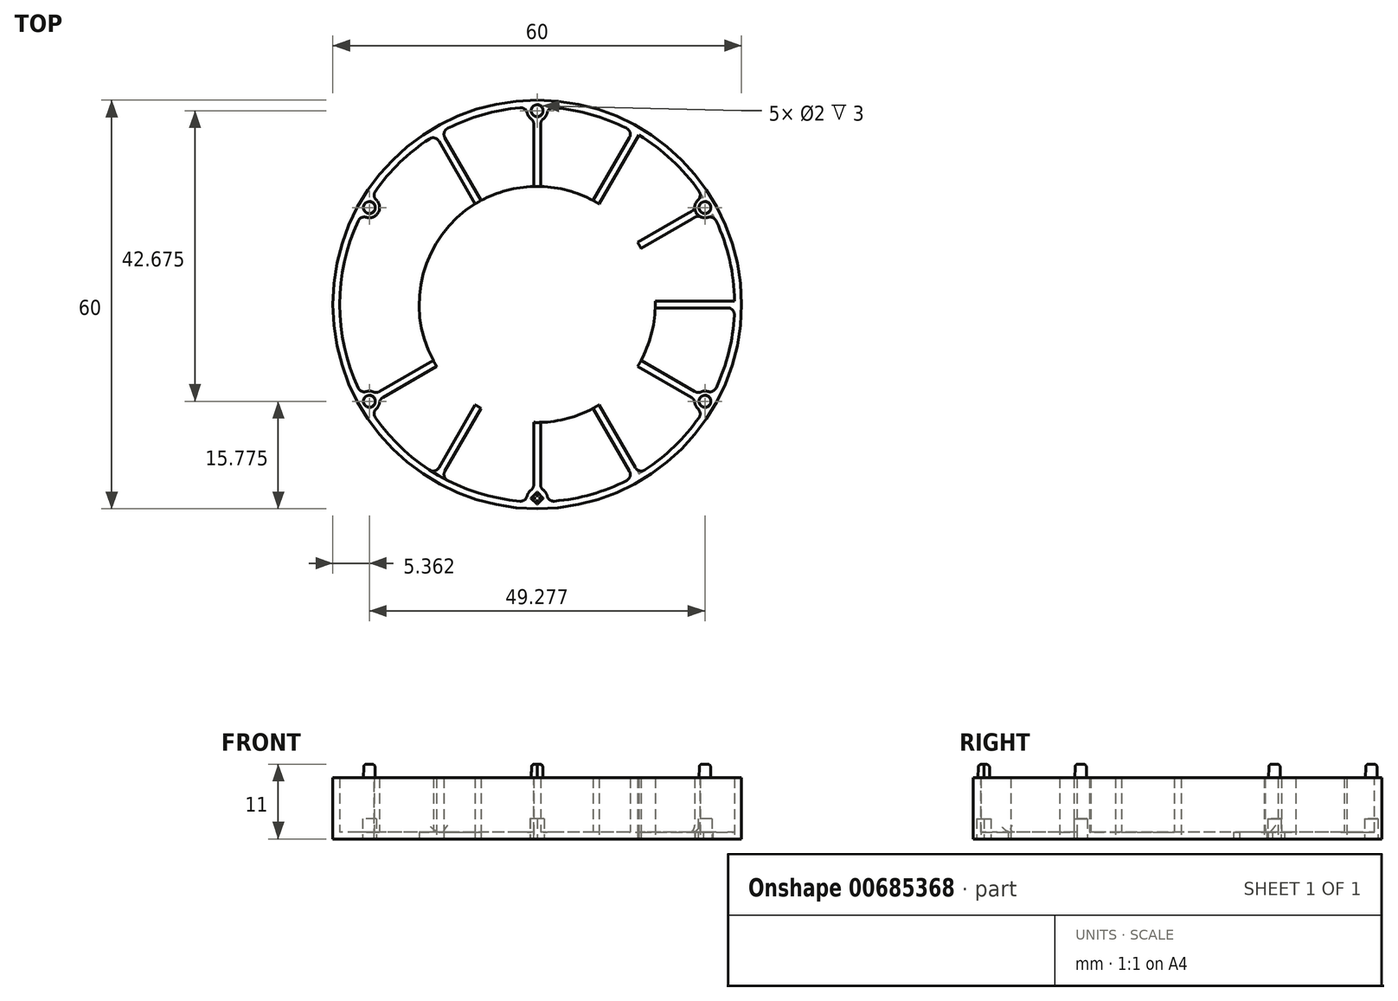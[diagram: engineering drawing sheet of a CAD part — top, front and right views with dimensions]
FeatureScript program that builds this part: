
annotation { "Feature Type Name" : "Feature", "Feature Type Description" : "" }
export const myFeature = defineFeature(function(context is Context, id is Id, definition is map)
    precondition{}
    {
        {
            var Q0;
            Q0=qCreatedBy(makeId("Top.planeOp"),FACE);
            var sketch = newSketch(context, id + "F0", { "sketchPlane" : qUnion([Q0])});
            skCircle(sketch, "E0", {"center": v(0, 0) * mm, "radius": 30 * mm});
            skCircle(sketch, "E1.0", {"center": v(0, 0) * mm, "radius": 29 * mm});
            skLineSegment(sketch, "E2.bottom", {"start": v(14.56, 26.23) * mm, "end": v(15.43, 25.73) * mm});
            skLineSegment(sketch, "E2.top", {"start": v(-15.43, -25.73) * mm, "end": v(-14.56, -26.23) * mm});
            skLineSegment(sketch, "E2.left", {"start": v(14.56, 26.23) * mm, "end": v(-15.43, -25.73) * mm});
            skLineSegment(sketch, "E2.right", {"start": v(15.43, 25.73) * mm, "end": v(-14.56, -26.23) * mm});
            skLineSegment(sketch, "E3.bottom", {"start": v(25.73, 15.43) * mm, "end": v(26.23, 14.56) * mm});
            skLineSegment(sketch, "E3.top", {"start": v(-26.23, -14.56) * mm, "end": v(-25.73, -15.43) * mm});
            skLineSegment(sketch, "E3.left", {"start": v(25.73, 15.43) * mm, "end": v(-26.23, -14.56) * mm});
            skLineSegment(sketch, "E3.right", {"start": v(26.23, 14.56) * mm, "end": v(-25.73, -15.43) * mm});
            skLineSegment(sketch, "E4", {"start": v(-38.35, 0) * mm, "end": v(39.17, 0) * mm, "construction": true});
            skLineSegment(sketch, "E5", {"start": v(0, 42.5) * mm, "end": v(0, -42.47) * mm, "construction": true});
            skLineSegment(sketch, "E6.bottom", {"start": v(-30, 0.5) * mm, "end": v(30, 0.5) * mm});
            skLineSegment(sketch, "E6.top", {"start": v(-30, -0.5) * mm, "end": v(30, -0.5) * mm});
            skLineSegment(sketch, "E6.left", {"start": v(-30, 0.5) * mm, "end": v(-30, -0.5) * mm});
            skLineSegment(sketch, "E6.right", {"start": v(30, 0.5) * mm, "end": v(30, -0.5) * mm});
            skLineSegment(sketch, "E7.bottom", {"start": v(-25.73, 15.43) * mm, "end": v(26.23, -14.56) * mm});
            skLineSegment(sketch, "E7.top", {"start": v(-26.23, 14.56) * mm, "end": v(25.73, -15.43) * mm});
            skLineSegment(sketch, "E7.left", {"start": v(-25.73, 15.43) * mm, "end": v(-26.23, 14.56) * mm});
            skLineSegment(sketch, "E7.right", {"start": v(26.23, -14.56) * mm, "end": v(25.73, -15.43) * mm});
            skLineSegment(sketch, "E8.bottom", {"start": v(-0.5, 30) * mm, "end": v(0.5, 30) * mm});
            skLineSegment(sketch, "E8.top", {"start": v(-0.5, -30) * mm, "end": v(0.5, -30) * mm});
            skLineSegment(sketch, "E8.left", {"start": v(-0.5, 30) * mm, "end": v(-0.5, -30) * mm});
            skLineSegment(sketch, "E8.right", {"start": v(0.5, 30) * mm, "end": v(0.5, -30) * mm});
            skLineSegment(sketch, "E9.bottom", {"start": v(-15.43, 25.73) * mm, "end": v(-14.56, 26.23) * mm});
            skLineSegment(sketch, "E9.top", {"start": v(14.56, -26.23) * mm, "end": v(15.43, -25.73) * mm});
            skLineSegment(sketch, "E9.left", {"start": v(-15.43, 25.73) * mm, "end": v(14.56, -26.23) * mm});
            skLineSegment(sketch, "E9.right", {"start": v(-14.56, 26.23) * mm, "end": v(15.43, -25.73) * mm});
            skCircle(sketch, "E10", {"center": v(0, 0) * mm, "radius": 17.33 * mm});
            skSolve(sketch);
        }
        {
            var Q0;
            Q0=qCreatedBy(makeId("Top.planeOp"),FACE);
            var sketch = newSketch(context, id + "F1", { "sketchPlane" : qUnion([Q0])});
            skCircle(sketch, "E11", {"center": v(0, 0) * mm, "radius": 30 * mm});
            skCircle(sketch, "E12", {"center": v(0, 0) * mm, "radius": 29 * mm});
            skSolve(sketch);
        }
        {
            var Q0;
            Q0=makeQuery(id+"F1.imprint","IMPRINT",FACE,{"disambiguationData":[TD([[makeQuery(id+"F1.imprint","IMPRINT",EDGE,{"derivedFrom":sQuery(id+"F1.wireOp",EDGE,"E11")}),1.0]])]});
            extrude(context, id + "F2", {"entities" : qUnion([Q0]), "depth" : 9 * mm, "offsetDistance" : 25 * mm});
        }
        {
            var Q0;
            {var subQ0=sQuery(id+"F0.wireOp",EDGE,"E2.right");var subQ1=sQuery(id+"F0.wireOp",EDGE,"E1.0");var subQ2=makeQuery(id+"F0.imprint","INTERSECT",VERTEX,{"disambiguationData":[OD(0.0)],"derivedFrom":[subQ1,subQ0]});Q0=makeQuery(id+"F0.imprint","IMPRINT",FACE,{"disambiguationData":[TD([[makeQuery(id+"F0.imprint","IMPRINT",EDGE,{"disambiguationData":[TD([[subQ2,-1.0]])],"derivedFrom":subQ1}),1.0]])]});}
            var Q1;
            {var subQ0=sQuery(id+"F0.wireOp",EDGE,"E6.bottom");var subQ1=sQuery(id+"F0.wireOp",EDGE,"E1.0");var subQ2=makeQuery(id+"F0.imprint","INTERSECT",VERTEX,{"disambiguationData":[OD(0.0)],"derivedFrom":[subQ1,subQ0]});Q1=makeQuery(id+"F0.imprint","IMPRINT",FACE,{"disambiguationData":[TD([[makeQuery(id+"F0.imprint","IMPRINT",EDGE,{"disambiguationData":[TD([[subQ2,1.0]])],"derivedFrom":subQ1}),1.0]])]});}
            var Q2;
            {var subQ0=sQuery(id+"F0.wireOp",EDGE,"E8.left");var subQ1=sQuery(id+"F0.wireOp",EDGE,"E1.0");var subQ2=makeQuery(id+"F0.imprint","INTERSECT",VERTEX,{"disambiguationData":[OD(1.0)],"derivedFrom":[subQ1,subQ0]});Q2=makeQuery(id+"F0.imprint","IMPRINT",FACE,{"disambiguationData":[TD([[makeQuery(id+"F0.imprint","IMPRINT",EDGE,{"disambiguationData":[TD([[subQ2,-1.0]])],"derivedFrom":subQ1}),1.0]])]});}
            var Q3;
            {var subQ0=sQuery(id+"F0.wireOp",EDGE,"E3.left");var subQ1=sQuery(id+"F0.wireOp",EDGE,"E1.0");var subQ2=makeQuery(id+"F0.imprint","INTERSECT",VERTEX,{"disambiguationData":[OD(1.0)],"derivedFrom":[subQ1,subQ0]});Q3=makeQuery(id+"F0.imprint","IMPRINT",FACE,{"disambiguationData":[TD([[makeQuery(id+"F0.imprint","IMPRINT",EDGE,{"disambiguationData":[TD([[subQ2,-1.0]])],"derivedFrom":subQ1}),1.0]])]});}
            var Q4;
            {var subQ0=sQuery(id+"F0.wireOp",EDGE,"E9.right");var subQ1=sQuery(id+"F0.wireOp",EDGE,"E1.0");var subQ2=makeQuery(id+"F0.imprint","INTERSECT",VERTEX,{"disambiguationData":[OD(0.0)],"derivedFrom":[subQ1,subQ0]});Q4=makeQuery(id+"F0.imprint","IMPRINT",FACE,{"disambiguationData":[TD([[makeQuery(id+"F0.imprint","IMPRINT",EDGE,{"disambiguationData":[TD([[subQ2,-1.0]])],"derivedFrom":subQ1}),1.0]])]});}
            var Q5;
            {var subQ0=sQuery(id+"F0.wireOp",EDGE,"E8.right");var subQ1=sQuery(id+"F0.wireOp",EDGE,"E1.0");var subQ2=makeQuery(id+"F0.imprint","INTERSECT",VERTEX,{"disambiguationData":[OD(0.0)],"derivedFrom":[subQ1,subQ0]});Q5=makeQuery(id+"F0.imprint","IMPRINT",FACE,{"disambiguationData":[TD([[makeQuery(id+"F0.imprint","IMPRINT",EDGE,{"disambiguationData":[TD([[subQ2,-1.0]])],"derivedFrom":subQ1}),1.0]])]});}
            var Q6;
            {var subQ0=sQuery(id+"F0.wireOp",EDGE,"E7.top");var subQ1=sQuery(id+"F0.wireOp",EDGE,"E1.0");var subQ2=makeQuery(id+"F0.imprint","INTERSECT",VERTEX,{"disambiguationData":[OD(1.0)],"derivedFrom":[subQ1,subQ0]});Q6=makeQuery(id+"F0.imprint","IMPRINT",FACE,{"disambiguationData":[TD([[makeQuery(id+"F0.imprint","IMPRINT",EDGE,{"disambiguationData":[TD([[subQ2,-1.0]])],"derivedFrom":subQ1}),1.0]])]});}
            var Q7;
            {var subQ0=sQuery(id+"F0.wireOp",EDGE,"E9.left");var subQ1=sQuery(id+"F0.wireOp",EDGE,"E1.0");var subQ2=makeQuery(id+"F0.imprint","INTERSECT",VERTEX,{"disambiguationData":[OD(1.0)],"derivedFrom":[subQ1,subQ0]});Q7=makeQuery(id+"F0.imprint","IMPRINT",FACE,{"disambiguationData":[TD([[makeQuery(id+"F0.imprint","IMPRINT",EDGE,{"disambiguationData":[TD([[subQ2,-1.0]])],"derivedFrom":subQ1}),1.0]])]});}
            extrude(context, id + "F3", {"entities" : qUnion([Q0, Q1, Q2, Q3, Q4, Q5, Q6, Q7]), "operationType" : NewBodyOperationType.ADD, "depth" : 9 * mm, "offsetDistance" : 25 * mm});
        }
        {
            var Q0;
            Q0=makeQuery(id+"F1.imprint","IMPRINT",FACE,{"disambiguationData":[TD([[makeQuery(id+"F1.imprint","IMPRINT",EDGE,{"derivedFrom":sQuery(id+"F1.wireOp",EDGE,"E11")}),1.0]])]});
            var Q1;
            Q1=makeQuery(id+"F1.imprint","IMPRINT",FACE,{"disambiguationData":[TD([[makeQuery(id+"F1.imprint","IMPRINT",EDGE,{"derivedFrom":sQuery(id+"F1.wireOp",EDGE,"E12")}),1.0]])]});
            extrude(context, id + "F4", {"entities" : qUnion([Q0, Q1]), "operationType" : NewBodyOperationType.ADD, "depth" : 1 * mm, "offsetDistance" : 25 * mm});
        }
        {
            var Q0;
            {var subQ0=sQuery(id+"F0.wireOp",EDGE,"E9.right");var subQ1=sQuery(id+"F0.wireOp",EDGE,"E1.0");var subQ2=makeQuery(id+"F0.imprint","INTERSECT",VERTEX,{"disambiguationData":[OD(1.0)],"derivedFrom":[subQ1,subQ0]});Q0=makeQuery(id+"F0.imprint","IMPRINT",FACE,{"disambiguationData":[TD([[makeQuery(id+"F0.imprint","IMPRINT",EDGE,{"disambiguationData":[TD([[subQ2,-1.0]])],"derivedFrom":subQ1}),1.0]])]});}
            var Q1;
            {var subQ0=sQuery(id+"F0.wireOp",EDGE,"E3.right");var subQ1=sQuery(id+"F0.wireOp",EDGE,"E1.0");var subQ2=makeQuery(id+"F0.imprint","INTERSECT",VERTEX,{"disambiguationData":[OD(0.0)],"derivedFrom":[subQ1,subQ0]});Q1=makeQuery(id+"F0.imprint","IMPRINT",FACE,{"disambiguationData":[TD([[makeQuery(id+"F0.imprint","IMPRINT",EDGE,{"disambiguationData":[TD([[subQ2,1.0]])],"derivedFrom":subQ1}),1.0]])]});}
            var Q2;
            {var subQ0=sQuery(id+"F0.wireOp",EDGE,"E3.left");var subQ1=sQuery(id+"F0.wireOp",EDGE,"E1.0");var subQ2=makeQuery(id+"F0.imprint","INTERSECT",VERTEX,{"disambiguationData":[OD(0.0)],"derivedFrom":[subQ1,subQ0]});Q2=makeQuery(id+"F0.imprint","IMPRINT",FACE,{"disambiguationData":[TD([[makeQuery(id+"F0.imprint","IMPRINT",EDGE,{"disambiguationData":[TD([[subQ2,-1.0]])],"derivedFrom":subQ1}),1.0]])]});}
            var Q3;
            {var subQ0=sQuery(id+"F0.wireOp",EDGE,"E3.right");var subQ1=sQuery(id+"F0.wireOp",EDGE,"E1.0");var subQ2=makeQuery(id+"F0.imprint","INTERSECT",VERTEX,{"disambiguationData":[OD(1.0)],"derivedFrom":[subQ1,subQ0]});Q3=makeQuery(id+"F0.imprint","IMPRINT",FACE,{"disambiguationData":[TD([[makeQuery(id+"F0.imprint","IMPRINT",EDGE,{"disambiguationData":[TD([[subQ2,-1.0]])],"derivedFrom":subQ1}),1.0]])]});}
            var Q4;
            {var subQ0=sQuery(id+"F0.wireOp",EDGE,"E2.right");var subQ1=sQuery(id+"F0.wireOp",EDGE,"E1.0");var subQ2=makeQuery(id+"F0.imprint","INTERSECT",VERTEX,{"disambiguationData":[OD(1.0)],"derivedFrom":[subQ1,subQ0]});Q4=makeQuery(id+"F0.imprint","IMPRINT",FACE,{"disambiguationData":[TD([[makeQuery(id+"F0.imprint","IMPRINT",EDGE,{"disambiguationData":[TD([[subQ2,-1.0]])],"derivedFrom":subQ1}),1.0]])]});}
            extrude(context, id + "F5", {"entities" : qUnion([Q0, Q1, Q2, Q3, Q4]), "operationType" : NewBodyOperationType.REMOVE, "depth" : 1 * mm, "offsetDistance" : 25 * mm});
        }
        {
            var Q0;
            Q0=qCreatedBy(makeId("Top.planeOp"),FACE);
            var sketch = newSketch(context, id + "F6", { "sketchPlane" : qUnion([Q0])});
            skCircle(sketch, "E13", {"center": v(0, 0) * mm, "radius": 28.45 * mm});
            skLineSegment(sketch, "E14", {"start": v(0, 28.45) * mm, "end": v(0, -28.45) * mm, "construction": true});
            skLineSegment(sketch, "E15", {"start": v(24.64, 14.22) * mm, "end": v(0, 0) * mm, "construction": true});
            skLineSegment(sketch, "E16", {"start": v(14.23, 24.64) * mm, "end": v(0, 0) * mm, "construction": true});
            skLineSegment(sketch, "E17", {"start": v(0, 0) * mm, "end": v(28.45, 0) * mm, "construction": true});
            skLineSegment(sketch, "E18", {"start": v(0, 0) * mm, "end": v(24.64, -14.22) * mm, "construction": true});
            skLineSegment(sketch, "E19", {"start": v(0, 0) * mm, "end": v(14.23, -24.64) * mm, "construction": true});
            skLineSegment(sketch, "E20", {"start": v(0, 0) * mm, "end": v(-14.23, 24.64) * mm, "construction": true});
            skLineSegment(sketch, "E21", {"start": v(0, 0) * mm, "end": v(-24.64, 14.22) * mm, "construction": true});
            skLineSegment(sketch, "E22", {"start": v(0, 0) * mm, "end": v(-28.45, 0) * mm, "construction": true});
            skLineSegment(sketch, "E23", {"start": v(0, 0) * mm, "end": v(-24.64, -14.23) * mm, "construction": true});
            skLineSegment(sketch, "E24", {"start": v(0, 0) * mm, "end": v(-14.22, -24.64) * mm, "construction": true});
            skCircle(sketch, "E25", {"center": v(0, 28.45) * mm, "radius": 1.5 * mm});
            skCircle(sketch, "E26", {"center": v(24.64, 14.22) * mm, "radius": 1.5 * mm});
            skCircle(sketch, "E27", {"center": v(24.64, -14.22) * mm, "radius": 1.5 * mm});
            skCircle(sketch, "E28", {"center": v(0, -28.45) * mm, "radius": 1.5 * mm});
            skCircle(sketch, "E29", {"center": v(-24.64, -14.23) * mm, "radius": 1.5 * mm});
            skCircle(sketch, "E30", {"center": v(-24.64, 14.22) * mm, "radius": 1.5 * mm});
            skCircle(sketch, "E31", {"center": v(-24.64, 14.22) * mm, "radius": 1 * mm});
            skCircle(sketch, "E32", {"center": v(0, 28.45) * mm, "radius": 1 * mm});
            skCircle(sketch, "E33", {"center": v(24.64, 14.22) * mm, "radius": 1 * mm});
            skCircle(sketch, "E34", {"center": v(24.64, -14.22) * mm, "radius": 1 * mm});
            skCircle(sketch, "E35", {"center": v(-24.64, -14.23) * mm, "radius": 1 * mm});
            skLineSegment(sketch, "E36.bottom", {"start": v(1.06, -28.45) * mm, "end": v(0, -29.51) * mm});
            skLineSegment(sketch, "E36.top", {"start": v(0, -27.39) * mm, "end": v(-1.06, -28.45) * mm});
            skLineSegment(sketch, "E36.left", {"start": v(1.06, -28.45) * mm, "end": v(0, -27.39) * mm});
            skLineSegment(sketch, "E36.right", {"start": v(0, -29.51) * mm, "end": v(-1.06, -28.45) * mm});
            skSolve(sketch);
        }
        {
            var Q0;
            {var subQ0=sQuery(id+"F6.wireOp",EDGE,"E30");var subQ1=sQuery(id+"F6.wireOp",EDGE,"E13");var subQ2=makeQuery(id+"F6.imprint","INTERSECT",VERTEX,{"disambiguationData":[OD(0.0)],"derivedFrom":[subQ1,subQ0]});Q0=makeQuery(id+"F6.imprint","IMPRINT",FACE,{"disambiguationData":[TD([[makeQuery(id+"F6.imprint","IMPRINT",EDGE,{"disambiguationData":[TD([[subQ2,-1.0]])],"derivedFrom":subQ1}),1.0]])]});}
            var Q1;
            {var subQ0=sQuery(id+"F6.wireOp",EDGE,"E30");var subQ1=sQuery(id+"F6.wireOp",EDGE,"E13");var subQ2=makeQuery(id+"F6.imprint","INTERSECT",VERTEX,{"disambiguationData":[OD(0.0)],"derivedFrom":[subQ1,subQ0]});Q1=makeQuery(id+"F6.imprint","IMPRINT",FACE,{"disambiguationData":[TD([[makeQuery(id+"F6.imprint","IMPRINT",EDGE,{"disambiguationData":[TD([[subQ2,-1.0]])],"derivedFrom":subQ1}),-1.0]])]});}
            var Q2;
            {var subQ0=sQuery(id+"F6.wireOp",EDGE,"E25");var subQ1=sQuery(id+"F6.wireOp",EDGE,"E13");var subQ2=makeQuery(id+"F6.imprint","INTERSECT",VERTEX,{"disambiguationData":[OD(0.0)],"derivedFrom":[subQ1,subQ0]});Q2=makeQuery(id+"F6.imprint","IMPRINT",FACE,{"disambiguationData":[TD([[makeQuery(id+"F6.imprint","IMPRINT",EDGE,{"disambiguationData":[TD([[subQ2,-1.0]])],"derivedFrom":subQ1}),1.0]])]});}
            var Q3;
            {var subQ0=sQuery(id+"F6.wireOp",EDGE,"E25");var subQ1=sQuery(id+"F6.wireOp",EDGE,"E13");var subQ2=makeQuery(id+"F6.imprint","INTERSECT",VERTEX,{"disambiguationData":[OD(0.0)],"derivedFrom":[subQ1,subQ0]});Q3=makeQuery(id+"F6.imprint","IMPRINT",FACE,{"disambiguationData":[TD([[makeQuery(id+"F6.imprint","IMPRINT",EDGE,{"disambiguationData":[TD([[subQ2,-1.0]])],"derivedFrom":subQ1}),-1.0]])]});}
            var Q4;
            {var subQ0=sQuery(id+"F6.wireOp",EDGE,"E26");var subQ1=sQuery(id+"F6.wireOp",EDGE,"E13");var subQ2=makeQuery(id+"F6.imprint","INTERSECT",VERTEX,{"disambiguationData":[OD(0.0)],"derivedFrom":[subQ1,subQ0]});Q4=makeQuery(id+"F6.imprint","IMPRINT",FACE,{"disambiguationData":[TD([[makeQuery(id+"F6.imprint","IMPRINT",EDGE,{"disambiguationData":[TD([[subQ2,-1.0]])],"derivedFrom":subQ1}),-1.0]])]});}
            var Q5;
            {var subQ0=sQuery(id+"F6.wireOp",EDGE,"E26");var subQ1=sQuery(id+"F6.wireOp",EDGE,"E13");var subQ2=makeQuery(id+"F6.imprint","INTERSECT",VERTEX,{"disambiguationData":[OD(0.0)],"derivedFrom":[subQ1,subQ0]});Q5=makeQuery(id+"F6.imprint","IMPRINT",FACE,{"disambiguationData":[TD([[makeQuery(id+"F6.imprint","IMPRINT",EDGE,{"disambiguationData":[TD([[subQ2,-1.0]])],"derivedFrom":subQ1}),1.0]])]});}
            var Q6;
            {var subQ0=sQuery(id+"F6.wireOp",EDGE,"E29");var subQ1=sQuery(id+"F6.wireOp",EDGE,"E13");var subQ2=makeQuery(id+"F6.imprint","INTERSECT",VERTEX,{"disambiguationData":[OD(0.0)],"derivedFrom":[subQ1,subQ0]});Q6=makeQuery(id+"F6.imprint","IMPRINT",FACE,{"disambiguationData":[TD([[makeQuery(id+"F6.imprint","IMPRINT",EDGE,{"disambiguationData":[TD([[subQ2,-1.0]])],"derivedFrom":subQ1}),1.0]])]});}
            var Q7;
            {var subQ0=sQuery(id+"F6.wireOp",EDGE,"E29");var subQ1=sQuery(id+"F6.wireOp",EDGE,"E13");var subQ2=makeQuery(id+"F6.imprint","INTERSECT",VERTEX,{"disambiguationData":[OD(0.0)],"derivedFrom":[subQ1,subQ0]});Q7=makeQuery(id+"F6.imprint","IMPRINT",FACE,{"disambiguationData":[TD([[makeQuery(id+"F6.imprint","IMPRINT",EDGE,{"disambiguationData":[TD([[subQ2,-1.0]])],"derivedFrom":subQ1}),-1.0]])]});}
            var Q8;
            {var subQ3=sQuery(id+"F6.wireOp",EDGE,"E13");var subQ5=sQuery(id+"F6.wireOp",EDGE,"E28");var subQ6=makeQuery(id+"F6.imprint","INTERSECT",VERTEX,{"disambiguationData":[OD(0.0)],"derivedFrom":[subQ3,subQ5]});Q8=makeQuery(id+"F6.imprint","IMPRINT",FACE,{"disambiguationData":[TD([[makeQuery(id+"F6.imprint","IMPRINT",EDGE,{"disambiguationData":[TD([[subQ6,-1.0]])],"derivedFrom":subQ3}),1.0]])]});}
            var Q9;
            {var subQ6=sQuery(id+"F6.wireOp",EDGE,"E36.bottom");Q9=makeQuery(id+"F6.imprint","IMPRINT",FACE,{"disambiguationData":[TD([[makeQuery(id+"F6.imprint","IMPRINT",EDGE,{"derivedFrom":subQ6}),1.0]])]});}
            var Q10;
            {var subQ0=sQuery(id+"F6.wireOp",EDGE,"E27");var subQ1=sQuery(id+"F6.wireOp",EDGE,"E13");var subQ2=makeQuery(id+"F6.imprint","INTERSECT",VERTEX,{"disambiguationData":[OD(0.0)],"derivedFrom":[subQ1,subQ0]});Q10=makeQuery(id+"F6.imprint","IMPRINT",FACE,{"disambiguationData":[TD([[makeQuery(id+"F6.imprint","IMPRINT",EDGE,{"disambiguationData":[TD([[subQ2,-1.0]])],"derivedFrom":subQ1}),-1.0]])]});}
            var Q11;
            {var subQ0=sQuery(id+"F6.wireOp",EDGE,"E27");var subQ1=sQuery(id+"F6.wireOp",EDGE,"E13");var subQ2=makeQuery(id+"F6.imprint","INTERSECT",VERTEX,{"disambiguationData":[OD(0.0)],"derivedFrom":[subQ1,subQ0]});Q11=makeQuery(id+"F6.imprint","IMPRINT",FACE,{"disambiguationData":[TD([[makeQuery(id+"F6.imprint","IMPRINT",EDGE,{"disambiguationData":[TD([[subQ2,-1.0]])],"derivedFrom":subQ1}),1.0]])]});}
            var Q12;
            {var subQ0=sQuery(id+"F6.wireOp",EDGE,"E31");var subQ1=sQuery(id+"F6.wireOp",EDGE,"E13");var subQ2=makeQuery(id+"F6.imprint","INTERSECT",VERTEX,{"disambiguationData":[OD(0.0)],"derivedFrom":[subQ1,subQ0]});Q12=makeQuery(id+"F6.imprint","IMPRINT",FACE,{"disambiguationData":[TD([[makeQuery(id+"F6.imprint","IMPRINT",EDGE,{"disambiguationData":[TD([[subQ2,-1.0]])],"derivedFrom":subQ1}),1.0]])]});}
            var Q13;
            {var subQ0=sQuery(id+"F6.wireOp",EDGE,"E31");var subQ1=sQuery(id+"F6.wireOp",EDGE,"E13");var subQ2=makeQuery(id+"F6.imprint","INTERSECT",VERTEX,{"disambiguationData":[OD(0.0)],"derivedFrom":[subQ1,subQ0]});Q13=makeQuery(id+"F6.imprint","IMPRINT",FACE,{"disambiguationData":[TD([[makeQuery(id+"F6.imprint","IMPRINT",EDGE,{"disambiguationData":[TD([[subQ2,-1.0]])],"derivedFrom":subQ1}),-1.0]])]});}
            var Q14;
            {var subQ0=sQuery(id+"F6.wireOp",EDGE,"E32");var subQ1=sQuery(id+"F6.wireOp",EDGE,"E13");var subQ2=makeQuery(id+"F6.imprint","INTERSECT",VERTEX,{"disambiguationData":[OD(0.0)],"derivedFrom":[subQ1,subQ0]});Q14=makeQuery(id+"F6.imprint","IMPRINT",FACE,{"disambiguationData":[TD([[makeQuery(id+"F6.imprint","IMPRINT",EDGE,{"disambiguationData":[TD([[subQ2,-1.0]])],"derivedFrom":subQ1}),-1.0]])]});}
            var Q15;
            {var subQ0=sQuery(id+"F6.wireOp",EDGE,"E32");var subQ1=sQuery(id+"F6.wireOp",EDGE,"E13");var subQ2=makeQuery(id+"F6.imprint","INTERSECT",VERTEX,{"disambiguationData":[OD(0.0)],"derivedFrom":[subQ1,subQ0]});Q15=makeQuery(id+"F6.imprint","IMPRINT",FACE,{"disambiguationData":[TD([[makeQuery(id+"F6.imprint","IMPRINT",EDGE,{"disambiguationData":[TD([[subQ2,-1.0]])],"derivedFrom":subQ1}),1.0]])]});}
            var Q16;
            {var subQ0=sQuery(id+"F6.wireOp",EDGE,"E33");var subQ1=sQuery(id+"F6.wireOp",EDGE,"E13");var subQ2=makeQuery(id+"F6.imprint","INTERSECT",VERTEX,{"disambiguationData":[OD(0.0)],"derivedFrom":[subQ1,subQ0]});Q16=makeQuery(id+"F6.imprint","IMPRINT",FACE,{"disambiguationData":[TD([[makeQuery(id+"F6.imprint","IMPRINT",EDGE,{"disambiguationData":[TD([[subQ2,-1.0]])],"derivedFrom":subQ1}),-1.0]])]});}
            var Q17;
            {var subQ0=sQuery(id+"F6.wireOp",EDGE,"E33");var subQ1=sQuery(id+"F6.wireOp",EDGE,"E13");var subQ2=makeQuery(id+"F6.imprint","INTERSECT",VERTEX,{"disambiguationData":[OD(0.0)],"derivedFrom":[subQ1,subQ0]});Q17=makeQuery(id+"F6.imprint","IMPRINT",FACE,{"disambiguationData":[TD([[makeQuery(id+"F6.imprint","IMPRINT",EDGE,{"disambiguationData":[TD([[subQ2,-1.0]])],"derivedFrom":subQ1}),1.0]])]});}
            var Q18;
            {var subQ0=sQuery(id+"F6.wireOp",EDGE,"E34");var subQ1=sQuery(id+"F6.wireOp",EDGE,"E13");var subQ2=makeQuery(id+"F6.imprint","INTERSECT",VERTEX,{"disambiguationData":[OD(0.0)],"derivedFrom":[subQ1,subQ0]});Q18=makeQuery(id+"F6.imprint","IMPRINT",FACE,{"disambiguationData":[TD([[makeQuery(id+"F6.imprint","IMPRINT",EDGE,{"disambiguationData":[TD([[subQ2,-1.0]])],"derivedFrom":subQ1}),-1.0]])]});}
            var Q19;
            {var subQ0=sQuery(id+"F6.wireOp",EDGE,"E34");var subQ1=sQuery(id+"F6.wireOp",EDGE,"E13");var subQ2=makeQuery(id+"F6.imprint","INTERSECT",VERTEX,{"disambiguationData":[OD(0.0)],"derivedFrom":[subQ1,subQ0]});Q19=makeQuery(id+"F6.imprint","IMPRINT",FACE,{"disambiguationData":[TD([[makeQuery(id+"F6.imprint","IMPRINT",EDGE,{"disambiguationData":[TD([[subQ2,-1.0]])],"derivedFrom":subQ1}),1.0]])]});}
            var Q20;
            {var subQ1=sQuery(id+"F6.wireOp",EDGE,"E36.bottom");Q20=makeQuery(id+"F6.imprint","IMPRINT",FACE,{"disambiguationData":[TD([[makeQuery(id+"F6.imprint","IMPRINT",EDGE,{"derivedFrom":subQ1}),-1.0]])]});}
            var Q21;
            {var subQ0=sQuery(id+"F6.wireOp",EDGE,"E35");var subQ1=sQuery(id+"F6.wireOp",EDGE,"E13");var subQ2=makeQuery(id+"F6.imprint","INTERSECT",VERTEX,{"disambiguationData":[OD(0.0)],"derivedFrom":[subQ1,subQ0]});Q21=makeQuery(id+"F6.imprint","IMPRINT",FACE,{"disambiguationData":[TD([[makeQuery(id+"F6.imprint","IMPRINT",EDGE,{"disambiguationData":[TD([[subQ2,-1.0]])],"derivedFrom":subQ1}),-1.0]])]});}
            var Q22;
            {var subQ0=sQuery(id+"F6.wireOp",EDGE,"E35");var subQ1=sQuery(id+"F6.wireOp",EDGE,"E13");var subQ2=makeQuery(id+"F6.imprint","INTERSECT",VERTEX,{"disambiguationData":[OD(0.0)],"derivedFrom":[subQ1,subQ0]});Q22=makeQuery(id+"F6.imprint","IMPRINT",FACE,{"disambiguationData":[TD([[makeQuery(id+"F6.imprint","IMPRINT",EDGE,{"disambiguationData":[TD([[subQ2,-1.0]])],"derivedFrom":subQ1}),1.0]])]});}
            var Q23;
            {var subQ0=sQuery(id+"F6.wireOp",EDGE,"E36.top");var subQ1=sQuery(id+"F6.wireOp",EDGE,"E13");var subQ2=makeQuery(id+"F6.imprint","INTERSECT",VERTEX,{"derivedFrom":[subQ1,subQ0]});Q23=makeQuery(id+"F6.imprint","IMPRINT",FACE,{"disambiguationData":[TD([[makeQuery(id+"F6.imprint","IMPRINT",EDGE,{"disambiguationData":[TD([[subQ2,-1.0]])],"derivedFrom":subQ1}),1.0]])]});}
            extrude(context, id + "F7", {"entities" : qUnion([Q0, Q1, Q2, Q3, Q4, Q5, Q6, Q7, Q8, Q9, Q10, Q11, Q12, Q13, Q14, Q15, Q16, Q17, Q18, Q19, Q20, Q21, Q22, Q23]), "operationType" : NewBodyOperationType.ADD, "depth" : 9 * mm, "offsetDistance" : 25 * mm});
        }
        {
            var Q0;
            {var subQ0=sQuery(id+"F0.wireOp",EDGE,"E8.right");var subQ1=sQuery(id+"F0.wireOp",EDGE,"E1.0");Q0=makeQuery(id+"F3.opExtrude","SWEPT_EDGE",EDGE,{"disambiguationData":[OSD([subQ1,subQ0]),TDD([makeQuery(id+"F0.imprint","INTERSECT",VERTEX,{"disambiguationData":[OD(1.0)],"derivedFrom":[subQ1,subQ0]})])]});}
            var Q1;
            {var subQ0=sQuery(id+"F0.wireOp",EDGE,"E2.left");var subQ1=sQuery(id+"F0.wireOp",EDGE,"E1.0");Q1=makeQuery(id+"F3.opExtrude","SWEPT_EDGE",EDGE,{"disambiguationData":[OSD([subQ1,subQ0]),TDD([makeQuery(id+"F0.imprint","INTERSECT",VERTEX,{"disambiguationData":[OD(1.0)],"derivedFrom":[subQ1,subQ0]})])]});}
            var Q2;
            {var subQ0=sQuery(id+"F0.wireOp",EDGE,"E3.left");var subQ1=sQuery(id+"F0.wireOp",EDGE,"E1.0");Q2=makeQuery(id+"F3.opExtrude","SWEPT_EDGE",EDGE,{"disambiguationData":[OSD([subQ1,subQ0]),TDD([makeQuery(id+"F0.imprint","INTERSECT",VERTEX,{"disambiguationData":[OD(1.0)],"derivedFrom":[subQ1,subQ0]})])]});}
            var Q3;
            {var subQ0=sQuery(id+"F0.wireOp",EDGE,"E6.bottom");var subQ1=sQuery(id+"F0.wireOp",EDGE,"E1.0");Q3=makeQuery(id+"F3.opExtrude","SWEPT_EDGE",EDGE,{"disambiguationData":[OSD([subQ1,subQ0]),TDD([makeQuery(id+"F0.imprint","INTERSECT",VERTEX,{"disambiguationData":[OD(1.0)],"derivedFrom":[subQ1,subQ0]})])]});}
            var Q4;
            {var subQ0=sQuery(id+"F0.wireOp",EDGE,"E9.right");var subQ1=sQuery(id+"F0.wireOp",EDGE,"E1.0");Q4=makeQuery(id+"F3.opExtrude","SWEPT_EDGE",EDGE,{"disambiguationData":[OSD([subQ1,subQ0]),TDD([makeQuery(id+"F0.imprint","INTERSECT",VERTEX,{"disambiguationData":[OD(1.0)],"derivedFrom":[subQ1,subQ0]})])]});}
            var Q5;
            {var subQ0=sQuery(id+"F0.wireOp",EDGE,"E7.bottom");var subQ1=sQuery(id+"F0.wireOp",EDGE,"E1.0");Q5=makeQuery(id+"F3.opExtrude","SWEPT_EDGE",EDGE,{"disambiguationData":[OSD([subQ1,subQ0]),TDD([makeQuery(id+"F0.imprint","INTERSECT",VERTEX,{"disambiguationData":[OD(1.0)],"derivedFrom":[subQ1,subQ0]})])]});}
            var Q6;
            {var subQ0=sQuery(id+"F0.wireOp",EDGE,"E8.left");var subQ1=sQuery(id+"F0.wireOp",EDGE,"E1.0");Q6=makeQuery(id+"F3.opExtrude","SWEPT_EDGE",EDGE,{"disambiguationData":[OSD([subQ1,subQ0]),TDD([makeQuery(id+"F0.imprint","INTERSECT",VERTEX,{"disambiguationData":[OD(0.0)],"derivedFrom":[subQ1,subQ0]})])]});}
            var Q7;
            {var subQ0=sQuery(id+"F0.wireOp",EDGE,"E2.left");var subQ1=sQuery(id+"F0.wireOp",EDGE,"E1.0");Q7=makeQuery(id+"F3.opExtrude","SWEPT_EDGE",EDGE,{"disambiguationData":[OSD([subQ1,subQ0]),TDD([makeQuery(id+"F0.imprint","INTERSECT",VERTEX,{"disambiguationData":[OD(0.0)],"derivedFrom":[subQ1,subQ0]})])]});}
            var Q8;
            {var subQ0=sQuery(id+"F0.wireOp",EDGE,"E3.left");var subQ1=sQuery(id+"F0.wireOp",EDGE,"E1.0");Q8=makeQuery(id+"F3.opExtrude","SWEPT_EDGE",EDGE,{"disambiguationData":[OSD([subQ1,subQ0]),TDD([makeQuery(id+"F0.imprint","INTERSECT",VERTEX,{"disambiguationData":[OD(0.0)],"derivedFrom":[subQ1,subQ0]})])]});}
            var Q9;
            {var subQ0=sQuery(id+"F0.wireOp",EDGE,"E6.top");var subQ1=sQuery(id+"F0.wireOp",EDGE,"E1.0");Q9=makeQuery(id+"F3.opExtrude","SWEPT_EDGE",EDGE,{"disambiguationData":[OSD([subQ1,subQ0]),TDD([makeQuery(id+"F0.imprint","INTERSECT",VERTEX,{"disambiguationData":[OD(1.0)],"derivedFrom":[subQ1,subQ0]})])]});}
            var Q10;
            {var subQ0=sQuery(id+"F0.wireOp",EDGE,"E7.top");var subQ1=sQuery(id+"F0.wireOp",EDGE,"E1.0");Q10=makeQuery(id+"F3.opExtrude","SWEPT_EDGE",EDGE,{"disambiguationData":[OSD([subQ1,subQ0]),TDD([makeQuery(id+"F0.imprint","INTERSECT",VERTEX,{"disambiguationData":[OD(0.0)],"derivedFrom":[subQ1,subQ0]})])]});}
            var Q11;
            {var subQ0=sQuery(id+"F0.wireOp",EDGE,"E6.top");var subQ1=sQuery(id+"F0.wireOp",EDGE,"E1.0");Q11=makeQuery(id+"F3.opExtrude","SWEPT_EDGE",EDGE,{"disambiguationData":[OSD([subQ1,subQ0]),TDD([makeQuery(id+"F0.imprint","INTERSECT",VERTEX,{"disambiguationData":[OD(0.0)],"derivedFrom":[subQ1,subQ0]})])]});}
            var Q12;
            {var subQ0=sQuery(id+"F0.wireOp",EDGE,"E9.left");var subQ1=sQuery(id+"F0.wireOp",EDGE,"E1.0");Q12=makeQuery(id+"F3.opExtrude","SWEPT_EDGE",EDGE,{"disambiguationData":[OSD([subQ1,subQ0]),TDD([makeQuery(id+"F0.imprint","INTERSECT",VERTEX,{"disambiguationData":[OD(0.0)],"derivedFrom":[subQ1,subQ0]})])]});}
            var Q13;
            {var subQ0=sQuery(id+"F0.wireOp",EDGE,"E8.right");var subQ1=sQuery(id+"F0.wireOp",EDGE,"E1.0");Q13=makeQuery(id+"F3.opExtrude","SWEPT_EDGE",EDGE,{"disambiguationData":[OSD([subQ1,subQ0]),TDD([makeQuery(id+"F0.imprint","INTERSECT",VERTEX,{"disambiguationData":[OD(0.0)],"derivedFrom":[subQ1,subQ0]})])]});}
            var Q14;
            {var subQ0=sQuery(id+"F0.wireOp",EDGE,"E7.bottom");var subQ1=sQuery(id+"F0.wireOp",EDGE,"E1.0");Q14=makeQuery(id+"F3.opExtrude","SWEPT_EDGE",EDGE,{"disambiguationData":[OSD([subQ1,subQ0]),TDD([makeQuery(id+"F0.imprint","INTERSECT",VERTEX,{"disambiguationData":[OD(0.0)],"derivedFrom":[subQ1,subQ0]})])]});}
            var Q15;
            {var subQ0=sQuery(id+"F0.wireOp",EDGE,"E9.right");var subQ1=sQuery(id+"F0.wireOp",EDGE,"E1.0");Q15=makeQuery(id+"F3.opExtrude","SWEPT_EDGE",EDGE,{"disambiguationData":[OSD([subQ1,subQ0]),TDD([makeQuery(id+"F0.imprint","INTERSECT",VERTEX,{"disambiguationData":[OD(0.0)],"derivedFrom":[subQ1,subQ0]})])]});}
            var Q16;
            {var subQ0=sQuery(id+"F0.wireOp",EDGE,"E3.right");var subQ1=sQuery(id+"F0.wireOp",EDGE,"E1.0");Q16=makeQuery(id+"F3.opExtrude","SWEPT_EDGE",EDGE,{"disambiguationData":[OSD([subQ1,subQ0]),TDD([makeQuery(id+"F0.imprint","INTERSECT",VERTEX,{"disambiguationData":[OD(1.0)],"derivedFrom":[subQ1,subQ0]})])]});}
            var Q17;
            {var subQ0=sQuery(id+"F0.wireOp",EDGE,"E2.right");var subQ1=sQuery(id+"F0.wireOp",EDGE,"E1.0");Q17=makeQuery(id+"F3.opExtrude","SWEPT_EDGE",EDGE,{"disambiguationData":[OSD([subQ1,subQ0]),TDD([makeQuery(id+"F0.imprint","INTERSECT",VERTEX,{"disambiguationData":[OD(1.0)],"derivedFrom":[subQ1,subQ0]})])]});}
            var Q18;
            {var subQ0=sQuery(id+"F0.wireOp",EDGE,"E3.right");var subQ1=sQuery(id+"F0.wireOp",EDGE,"E1.0");Q18=makeQuery(id+"F3.opExtrude","SWEPT_EDGE",EDGE,{"disambiguationData":[OSD([subQ1,subQ0]),TDD([makeQuery(id+"F0.imprint","INTERSECT",VERTEX,{"disambiguationData":[OD(0.0)],"derivedFrom":[subQ1,subQ0]})])]});}
            var Q19;
            {var subQ0=sQuery(id+"F0.wireOp",EDGE,"E2.right");var subQ1=sQuery(id+"F0.wireOp",EDGE,"E1.0");Q19=makeQuery(id+"F3.opExtrude","SWEPT_EDGE",EDGE,{"disambiguationData":[OSD([subQ1,subQ0]),TDD([makeQuery(id+"F0.imprint","INTERSECT",VERTEX,{"disambiguationData":[OD(0.0)],"derivedFrom":[subQ1,subQ0]})])]});}
            var Q20;
            {var subQ0=sQuery(id+"F0.wireOp",EDGE,"E8.left");var subQ1=sQuery(id+"F0.wireOp",EDGE,"E1.0");Q20=makeQuery(id+"F3.opExtrude","SWEPT_EDGE",EDGE,{"disambiguationData":[OSD([subQ1,subQ0]),TDD([makeQuery(id+"F0.imprint","INTERSECT",VERTEX,{"disambiguationData":[OD(1.0)],"derivedFrom":[subQ1,subQ0]})])]});}
            var Q21;
            {var subQ0=sQuery(id+"F0.wireOp",EDGE,"E9.left");var subQ1=sQuery(id+"F0.wireOp",EDGE,"E1.0");Q21=makeQuery(id+"F3.opExtrude","SWEPT_EDGE",EDGE,{"disambiguationData":[OSD([subQ1,subQ0]),TDD([makeQuery(id+"F0.imprint","INTERSECT",VERTEX,{"disambiguationData":[OD(1.0)],"derivedFrom":[subQ1,subQ0]})])]});}
            var Q22;
            {var subQ0=sQuery(id+"F0.wireOp",EDGE,"E7.top");var subQ1=sQuery(id+"F0.wireOp",EDGE,"E1.0");Q22=makeQuery(id+"F3.opExtrude","SWEPT_EDGE",EDGE,{"disambiguationData":[OSD([subQ1,subQ0]),TDD([makeQuery(id+"F0.imprint","INTERSECT",VERTEX,{"disambiguationData":[OD(1.0)],"derivedFrom":[subQ1,subQ0]})])]});}
            var Q23;
            {var subQ0=sQuery(id+"F0.wireOp",EDGE,"E6.bottom");var subQ1=sQuery(id+"F0.wireOp",EDGE,"E1.0");Q23=makeQuery(id+"F3.opExtrude","SWEPT_EDGE",EDGE,{"disambiguationData":[OSD([subQ1,subQ0]),TDD([makeQuery(id+"F0.imprint","INTERSECT",VERTEX,{"disambiguationData":[OD(0.0)],"derivedFrom":[subQ1,subQ0]})])]});}
            var Q24;
            {var subQ2=sQuery(id+"F0.wireOp",EDGE,"E3.left");var subQ24=sQuery(id+"F1.wireOp",EDGE,"E12");Q24=makeQuery(id+"F7.boolean.opBoolean","INTERSECT",EDGE,{"disambiguationData":[OD(1.0)],"derivedFrom":[makeQuery(id+"F3.boolean.opBoolean","SPLIT",FACE,{"disambiguationData":[TD([makeQuery(id+"F3.opExtrude","SWEPT_FACE",FACE,{"disambiguationData":[OSD([subQ2])]})])],"derivedFrom":makeQuery(id+"F2.opExtrude","SWEPT_FACE",FACE,{"disambiguationData":[OSD([subQ24])]})}),makeQuery(id+"F7.opExtrude","SWEPT_FACE",FACE,{"disambiguationData":[OSD([sQuery(id+"F6.wireOp",EDGE,"E30")])]})]});}
            var Q25;
            {var subQ2=sQuery(id+"F0.wireOp",EDGE,"E3.left");var subQ24=sQuery(id+"F1.wireOp",EDGE,"E12");Q25=makeQuery(id+"F7.boolean.opBoolean","INTERSECT",EDGE,{"disambiguationData":[OD(0.0)],"derivedFrom":[makeQuery(id+"F3.boolean.opBoolean","SPLIT",FACE,{"disambiguationData":[TD([makeQuery(id+"F3.opExtrude","SWEPT_FACE",FACE,{"disambiguationData":[OSD([subQ2])]})])],"derivedFrom":makeQuery(id+"F2.opExtrude","SWEPT_FACE",FACE,{"disambiguationData":[OSD([subQ24])]})}),makeQuery(id+"F7.opExtrude","SWEPT_FACE",FACE,{"disambiguationData":[OSD([sQuery(id+"F6.wireOp",EDGE,"E30")])]})]});}
            var Q26;
            {var subQ24=sQuery(id+"F1.wireOp",EDGE,"E12");var subQ35=sQuery(id+"F0.wireOp",EDGE,"E2.left");Q26=makeQuery(id+"F7.boolean.opBoolean","INTERSECT",EDGE,{"derivedFrom":[makeQuery(id+"F3.boolean.opBoolean","SPLIT",FACE,{"disambiguationData":[TD([makeQuery(id+"F3.opExtrude","SWEPT_FACE",FACE,{"disambiguationData":[OSD([subQ35])]})])],"derivedFrom":makeQuery(id+"F2.opExtrude","SWEPT_FACE",FACE,{"disambiguationData":[OSD([subQ24])]})}),makeQuery(id+"F7.opExtrude","SWEPT_FACE",FACE,{"disambiguationData":[OSD([sQuery(id+"F6.wireOp",EDGE,"E25")])]})]});}
            var Q27;
            {var subQ3=sQuery(id+"F0.wireOp",EDGE,"E1.0");var subQ14=sQuery(id+"F0.wireOp",EDGE,"E8.left");var subQ21=makeQuery(id+"F0.imprint","INTERSECT",VERTEX,{"disambiguationData":[OD(0.0)],"derivedFrom":[subQ3,subQ14]});var subQ22=makeQuery(id+"F0.imprint","IMPRINT",EDGE,{"disambiguationData":[TD([[subQ21,-1.0]])],"derivedFrom":subQ14});var subQ24=sQuery(id+"F1.wireOp",EDGE,"E12");Q27=makeQuery(id+"F7.boolean.opBoolean","INTERSECT",EDGE,{"derivedFrom":[makeQuery(id+"F3.boolean.opBoolean","SPLIT",FACE,{"disambiguationData":[TD([makeQuery(id+"F3.opExtrude","SWEPT_FACE",FACE,{"disambiguationData":[OSD([subQ14]),TDD([subQ22])]})])],"derivedFrom":makeQuery(id+"F2.opExtrude","SWEPT_FACE",FACE,{"disambiguationData":[OSD([subQ24])]})}),makeQuery(id+"F7.opExtrude","SWEPT_FACE",FACE,{"disambiguationData":[OSD([sQuery(id+"F6.wireOp",EDGE,"E25")])]})]});}
            var Q28;
            {var subQ0=sQuery(id+"F0.wireOp",EDGE,"E8.left");Q28=makeQuery(id+"F7.boolean.opBoolean","INTERSECT",EDGE,{"derivedFrom":[makeQuery(id+"F3.opExtrude","SWEPT_FACE",FACE,{"disambiguationData":[OSD([subQ0]),TDD([makeQuery(id+"F0.imprint","IMPRINT",EDGE,{"disambiguationData":[TD([[makeQuery(id+"F0.imprint","INTERSECT",VERTEX,{"disambiguationData":[OD(0.0)],"derivedFrom":[sQuery(id+"F0.wireOp",EDGE,"E1.0"),subQ0]}),-1.0]])],"derivedFrom":subQ0})])]}),makeQuery(id+"F7.opExtrude","SWEPT_FACE",FACE,{"disambiguationData":[OSD([sQuery(id+"F6.wireOp",EDGE,"E25")])]})]});}
            var Q29;
            {var subQ0=sQuery(id+"F0.wireOp",EDGE,"E8.right");Q29=makeQuery(id+"F7.boolean.opBoolean","INTERSECT",EDGE,{"derivedFrom":[makeQuery(id+"F3.opExtrude","SWEPT_FACE",FACE,{"disambiguationData":[OSD([subQ0]),TDD([makeQuery(id+"F0.imprint","IMPRINT",EDGE,{"disambiguationData":[TD([[makeQuery(id+"F0.imprint","INTERSECT",VERTEX,{"disambiguationData":[OD(0.0)],"derivedFrom":[sQuery(id+"F0.wireOp",EDGE,"E1.0"),subQ0]}),-1.0]])],"derivedFrom":subQ0})])]}),makeQuery(id+"F7.opExtrude","SWEPT_FACE",FACE,{"disambiguationData":[OSD([sQuery(id+"F6.wireOp",EDGE,"E25")])]})]});}
            var Q30;
            {var subQ0=sQuery(id+"F0.wireOp",EDGE,"E3.left");var subQ1=sQuery(id+"F0.wireOp",EDGE,"E1.0");var subQ2=sQuery(id+"F0.wireOp",EDGE,"E2.right");var subQ3=sQuery(id+"F0.wireOp",EDGE,"E3.right");var subQ26=sQuery(id+"F1.wireOp",EDGE,"E12");Q30=makeQuery(id+"F7.boolean.opBoolean","INTERSECT",EDGE,{"disambiguationData":[OD(1.0)],"derivedFrom":[makeQuery(id+"F5.boolean.opBoolean","MERGE",FACE,{"derivedFrom":[makeQuery(id+"F3.boolean.opBoolean","SPLIT",FACE,{"disambiguationData":[TD([makeQuery(id+"F3.opExtrude","SWEPT_FACE",FACE,{"disambiguationData":[OSD([subQ2])]})])],"derivedFrom":makeQuery(id+"F2.opExtrude","SWEPT_FACE",FACE,{"disambiguationData":[OSD([subQ26])]})}),makeQuery(id+"F5.opExtrude","SWEPT_FACE",FACE,{"disambiguationData":[OSD([subQ1]),TDD([makeQuery(id+"F0.imprint","IMPRINT",EDGE,{"disambiguationData":[TD([[makeQuery(id+"F0.imprint","INTERSECT",VERTEX,{"disambiguationData":[OD(0.0)],"derivedFrom":[subQ1,subQ3]}),1.0]])],"derivedFrom":subQ1})])]}),makeQuery(id+"F5.opExtrude","SWEPT_FACE",FACE,{"disambiguationData":[OSD([subQ1]),TDD([makeQuery(id+"F0.imprint","IMPRINT",EDGE,{"disambiguationData":[TD([[makeQuery(id+"F0.imprint","INTERSECT",VERTEX,{"disambiguationData":[OD(0.0)],"derivedFrom":[subQ1,subQ0]}),-1.0]])],"derivedFrom":subQ1})])]})]}),makeQuery(id+"F7.opExtrude","SWEPT_FACE",FACE,{"disambiguationData":[OSD([sQuery(id+"F6.wireOp",EDGE,"E26")])]})]});}
            var Q31;
            Q31=makeQuery(id+"F7.boolean.opBoolean","INTERSECT",EDGE,{"derivedFrom":[makeQuery(id+"F5.boolean.opBoolean","COPY",FACE,{"derivedFrom":makeQuery(id+"F5.opExtrude","SWEPT_FACE",FACE,{"disambiguationData":[OSD([sQuery(id+"F0.wireOp",EDGE,"E3.left")])]})}),makeQuery(id+"F7.opExtrude","SWEPT_FACE",FACE,{"disambiguationData":[OSD([sQuery(id+"F6.wireOp",EDGE,"E26")])]})]});
            var Q32;
            Q32=makeQuery(id+"F7.boolean.opBoolean","INTERSECT",EDGE,{"derivedFrom":[makeQuery(id+"F4.opExtrude","CAP_FACE",FACE,{"disambiguationData":[OSD([sQuery(id+"F1.wireOp",EDGE,"E11")])],"isStart":false}),makeQuery(id+"F7.opExtrude","SWEPT_FACE",FACE,{"disambiguationData":[OSD([sQuery(id+"F6.wireOp",EDGE,"E26")])]})]});
            var Q33;
            {var subQ0=sQuery(id+"F0.wireOp",EDGE,"E3.right");Q33=makeQuery(id+"F7.boolean.opBoolean","INTERSECT",EDGE,{"derivedFrom":[makeQuery(id+"F5.boolean.opBoolean","COPY",FACE,{"derivedFrom":makeQuery(id+"F5.opExtrude","SWEPT_FACE",FACE,{"disambiguationData":[OSD([subQ0]),TDD([makeQuery(id+"F0.imprint","IMPRINT",EDGE,{"disambiguationData":[TD([[makeQuery(id+"F0.imprint","INTERSECT",VERTEX,{"disambiguationData":[OD(0.0)],"derivedFrom":[sQuery(id+"F0.wireOp",EDGE,"E1.0"),subQ0]}),-1.0]])],"derivedFrom":subQ0})])]})}),makeQuery(id+"F7.opExtrude","SWEPT_FACE",FACE,{"disambiguationData":[OSD([sQuery(id+"F6.wireOp",EDGE,"E26")])]})]});}
            var Q34;
            {var subQ0=sQuery(id+"F0.wireOp",EDGE,"E3.left");var subQ1=sQuery(id+"F0.wireOp",EDGE,"E1.0");var subQ2=sQuery(id+"F0.wireOp",EDGE,"E2.right");var subQ3=sQuery(id+"F0.wireOp",EDGE,"E3.right");var subQ26=sQuery(id+"F1.wireOp",EDGE,"E12");Q34=makeQuery(id+"F7.boolean.opBoolean","INTERSECT",EDGE,{"disambiguationData":[OD(0.0)],"derivedFrom":[makeQuery(id+"F5.boolean.opBoolean","MERGE",FACE,{"derivedFrom":[makeQuery(id+"F3.boolean.opBoolean","SPLIT",FACE,{"disambiguationData":[TD([makeQuery(id+"F3.opExtrude","SWEPT_FACE",FACE,{"disambiguationData":[OSD([subQ2])]})])],"derivedFrom":makeQuery(id+"F2.opExtrude","SWEPT_FACE",FACE,{"disambiguationData":[OSD([subQ26])]})}),makeQuery(id+"F5.opExtrude","SWEPT_FACE",FACE,{"disambiguationData":[OSD([subQ1]),TDD([makeQuery(id+"F0.imprint","IMPRINT",EDGE,{"disambiguationData":[TD([[makeQuery(id+"F0.imprint","INTERSECT",VERTEX,{"disambiguationData":[OD(0.0)],"derivedFrom":[subQ1,subQ3]}),1.0]])],"derivedFrom":subQ1})])]}),makeQuery(id+"F5.opExtrude","SWEPT_FACE",FACE,{"disambiguationData":[OSD([subQ1]),TDD([makeQuery(id+"F0.imprint","IMPRINT",EDGE,{"disambiguationData":[TD([[makeQuery(id+"F0.imprint","INTERSECT",VERTEX,{"disambiguationData":[OD(0.0)],"derivedFrom":[subQ1,subQ0]}),-1.0]])],"derivedFrom":subQ1})])]})]}),makeQuery(id+"F7.opExtrude","SWEPT_FACE",FACE,{"disambiguationData":[OSD([sQuery(id+"F6.wireOp",EDGE,"E26")])]})]});}
            var Q35;
            {var subQ0=sQuery(id+"F0.wireOp",EDGE,"E7.top");Q35=makeQuery(id+"F7.boolean.opBoolean","INTERSECT",EDGE,{"derivedFrom":[makeQuery(id+"F5.boolean.opBoolean","MERGE",FACE,{"derivedFrom":[makeQuery(id+"F3.opExtrude","SWEPT_FACE",FACE,{"disambiguationData":[OSD([subQ0])]}),makeQuery(id+"F5.opExtrude","SWEPT_FACE",FACE,{"disambiguationData":[OSD([subQ0])]})]}),makeQuery(id+"F7.opExtrude","SWEPT_FACE",FACE,{"disambiguationData":[OSD([sQuery(id+"F6.wireOp",EDGE,"E27")])]})]});}
            var Q36;
            {var subQ0=sQuery(id+"F0.wireOp",EDGE,"E9.right");var subQ1=sQuery(id+"F0.wireOp",EDGE,"E1.0");var subQ2=makeQuery(id+"F0.imprint","INTERSECT",VERTEX,{"disambiguationData":[OD(1.0)],"derivedFrom":[subQ1,subQ0]});var subQ3=sQuery(id+"F0.wireOp",EDGE,"E7.top");var subQ26=sQuery(id+"F1.wireOp",EDGE,"E12");Q36=makeQuery(id+"F7.boolean.opBoolean","INTERSECT",EDGE,{"derivedFrom":[makeQuery(id+"F5.boolean.opBoolean","MERGE",FACE,{"derivedFrom":[makeQuery(id+"F3.boolean.opBoolean","SPLIT",FACE,{"disambiguationData":[TD([makeQuery(id+"F3.opExtrude","SWEPT_FACE",FACE,{"disambiguationData":[OSD([subQ3])]})])],"derivedFrom":makeQuery(id+"F2.opExtrude","SWEPT_FACE",FACE,{"disambiguationData":[OSD([subQ26])]})}),makeQuery(id+"F5.opExtrude","SWEPT_FACE",FACE,{"disambiguationData":[OSD([subQ1]),TDD([makeQuery(id+"F0.imprint","IMPRINT",EDGE,{"disambiguationData":[TD([[subQ2,-1.0]])],"derivedFrom":subQ1})])]})]}),makeQuery(id+"F7.opExtrude","SWEPT_FACE",FACE,{"disambiguationData":[OSD([sQuery(id+"F6.wireOp",EDGE,"E27")])]})]});}
            var Q37;
            {var subQ25=sQuery(id+"F1.wireOp",EDGE,"E12");var subQ46=sQuery(id+"F0.wireOp",EDGE,"E6.top");Q37=makeQuery(id+"F7.boolean.opBoolean","INTERSECT",EDGE,{"derivedFrom":[makeQuery(id+"F3.boolean.opBoolean","SPLIT",FACE,{"disambiguationData":[TD([makeQuery(id+"F3.opExtrude","SWEPT_FACE",FACE,{"disambiguationData":[OSD([subQ46])]})])],"derivedFrom":makeQuery(id+"F2.opExtrude","SWEPT_FACE",FACE,{"disambiguationData":[OSD([subQ25])]})}),makeQuery(id+"F7.opExtrude","SWEPT_FACE",FACE,{"disambiguationData":[OSD([sQuery(id+"F6.wireOp",EDGE,"E27")])]})]});}
            var Q38;
            Q38=makeQuery(id+"F7.boolean.opBoolean","INTERSECT",EDGE,{"derivedFrom":[makeQuery(id+"F3.opExtrude","SWEPT_FACE",FACE,{"disambiguationData":[OSD([sQuery(id+"F0.wireOp",EDGE,"E7.bottom")])]}),makeQuery(id+"F7.opExtrude","SWEPT_FACE",FACE,{"disambiguationData":[OSD([sQuery(id+"F6.wireOp",EDGE,"E27")])]})]});
            var Q39;
            {var subQ3=sQuery(id+"F0.wireOp",EDGE,"E1.0");var subQ16=sQuery(id+"F0.wireOp",EDGE,"E8.right");var subQ24=sQuery(id+"F1.wireOp",EDGE,"E12");var subQ39=makeQuery(id+"F0.imprint","INTERSECT",VERTEX,{"disambiguationData":[OD(1.0)],"derivedFrom":[subQ3,subQ16]});var subQ40=makeQuery(id+"F0.imprint","IMPRINT",EDGE,{"disambiguationData":[TD([[subQ39,1.0]])],"derivedFrom":subQ16});Q39=makeQuery(id+"F7.boolean.opBoolean","INTERSECT",EDGE,{"derivedFrom":[makeQuery(id+"F3.boolean.opBoolean","SPLIT",FACE,{"disambiguationData":[TD([makeQuery(id+"F3.opExtrude","SWEPT_FACE",FACE,{"disambiguationData":[OSD([subQ16]),TDD([subQ40])]})])],"derivedFrom":makeQuery(id+"F2.opExtrude","SWEPT_FACE",FACE,{"disambiguationData":[OSD([subQ24])]})}),makeQuery(id+"F7.opExtrude","SWEPT_FACE",FACE,{"disambiguationData":[OSD([sQuery(id+"F6.wireOp",EDGE,"E28")])]})]});}
            var Q40;
            {var subQ0=sQuery(id+"F0.wireOp",EDGE,"E8.right");Q40=makeQuery(id+"F7.boolean.opBoolean","INTERSECT",EDGE,{"derivedFrom":[makeQuery(id+"F3.opExtrude","SWEPT_FACE",FACE,{"disambiguationData":[OSD([subQ0]),TDD([makeQuery(id+"F0.imprint","IMPRINT",EDGE,{"disambiguationData":[TD([[makeQuery(id+"F0.imprint","INTERSECT",VERTEX,{"disambiguationData":[OD(1.0)],"derivedFrom":[sQuery(id+"F0.wireOp",EDGE,"E1.0"),subQ0]}),1.0]])],"derivedFrom":subQ0})])]}),makeQuery(id+"F7.opExtrude","SWEPT_FACE",FACE,{"disambiguationData":[OSD([sQuery(id+"F6.wireOp",EDGE,"E28")])]})]});}
            var Q41;
            {var subQ0=sQuery(id+"F0.wireOp",EDGE,"E2.right");var subQ1=sQuery(id+"F0.wireOp",EDGE,"E1.0");var subQ4=sQuery(id+"F0.wireOp",EDGE,"E3.right");var subQ29=sQuery(id+"F1.wireOp",EDGE,"E12");Q41=makeQuery(id+"F7.boolean.opBoolean","INTERSECT",EDGE,{"derivedFrom":[makeQuery(id+"F5.boolean.opBoolean","MERGE",FACE,{"derivedFrom":[makeQuery(id+"F3.boolean.opBoolean","SPLIT",FACE,{"disambiguationData":[TD([makeQuery(id+"F3.opExtrude","SWEPT_FACE",FACE,{"disambiguationData":[OSD([subQ4])]})])],"derivedFrom":makeQuery(id+"F2.opExtrude","SWEPT_FACE",FACE,{"disambiguationData":[OSD([subQ29])]})}),makeQuery(id+"F5.opExtrude","SWEPT_FACE",FACE,{"disambiguationData":[OSD([subQ1]),TDD([makeQuery(id+"F0.imprint","IMPRINT",EDGE,{"disambiguationData":[TD([[makeQuery(id+"F0.imprint","INTERSECT",VERTEX,{"disambiguationData":[OD(1.0)],"derivedFrom":[subQ1,subQ4]}),-1.0]])],"derivedFrom":subQ1})])]}),makeQuery(id+"F5.opExtrude","SWEPT_FACE",FACE,{"disambiguationData":[OSD([subQ1]),TDD([makeQuery(id+"F0.imprint","IMPRINT",EDGE,{"disambiguationData":[TD([[makeQuery(id+"F0.imprint","INTERSECT",VERTEX,{"disambiguationData":[OD(1.0)],"derivedFrom":[subQ1,subQ0]}),-1.0]])],"derivedFrom":subQ1})])]})]}),makeQuery(id+"F7.opExtrude","SWEPT_FACE",FACE,{"disambiguationData":[OSD([sQuery(id+"F6.wireOp",EDGE,"E28")])]})]});}
            var Q42;
            {var subQ0=sQuery(id+"F0.wireOp",EDGE,"E8.left");Q42=makeQuery(id+"F7.boolean.opBoolean","INTERSECT",EDGE,{"derivedFrom":[makeQuery(id+"F5.boolean.opBoolean","MERGE",FACE,{"derivedFrom":[makeQuery(id+"F3.opExtrude","SWEPT_FACE",FACE,{"disambiguationData":[OSD([subQ0]),TDD([makeQuery(id+"F0.imprint","IMPRINT",EDGE,{"disambiguationData":[TD([[makeQuery(id+"F0.imprint","INTERSECT",VERTEX,{"disambiguationData":[OD(1.0)],"derivedFrom":[sQuery(id+"F0.wireOp",EDGE,"E1.0"),subQ0]}),1.0]])],"derivedFrom":subQ0})])]}),makeQuery(id+"F5.opExtrude","SWEPT_FACE",FACE,{"disambiguationData":[OSD([subQ0])]})]}),makeQuery(id+"F7.opExtrude","SWEPT_FACE",FACE,{"disambiguationData":[OSD([sQuery(id+"F6.wireOp",EDGE,"E28")])]})]});}
            var Q43;
            Q43=makeQuery(id+"F5.boolean.opBoolean","COPY",EDGE,{"derivedFrom":makeQuery(id+"F5.opExtrude","SWEPT_EDGE",EDGE,{"disambiguationData":[OSD([sQuery(id+"F0.wireOp",EDGE,"E1.0"),sQuery(id+"F0.wireOp",EDGE,"E2.left")])]})});
            var Q44;
            {var subQ0=sQuery(id+"F1.wireOp",EDGE,"E11");var subQ2=sQuery(id+"F0.wireOp",EDGE,"E3.right");var subQ28=sQuery(id+"F1.wireOp",EDGE,"E12");Q44=makeQuery(id+"F4.boolean.opBoolean","INTERSECT",EDGE,{"derivedFrom":[makeQuery(id+"F3.boolean.opBoolean","SPLIT",FACE,{"disambiguationData":[TD([makeQuery(id+"F3.opExtrude","SWEPT_FACE",FACE,{"disambiguationData":[OSD([subQ2])]})])],"derivedFrom":makeQuery(id+"F2.opExtrude","SWEPT_FACE",FACE,{"disambiguationData":[OSD([subQ28])]})}),makeQuery(id+"F4.opExtrude","CAP_FACE",FACE,{"disambiguationData":[OSD([subQ0])],"isStart":false})]});}
            var Q45;
            {var subQ0=sQuery(id+"F0.wireOp",EDGE,"E2.right");var subQ1=sQuery(id+"F0.wireOp",EDGE,"E1.0");Q45=makeQuery(id+"F5.boolean.opBoolean","COPY",EDGE,{"derivedFrom":makeQuery(id+"F5.opExtrude","SWEPT_EDGE",EDGE,{"disambiguationData":[OSD([subQ1,subQ0]),TDD([makeQuery(id+"F0.imprint","INTERSECT",VERTEX,{"disambiguationData":[OD(1.0)],"derivedFrom":[subQ1,subQ0]})])]})});}
            var Q46;
            {var subQ0=sQuery(id+"F0.wireOp",EDGE,"E2.right");var subQ1=sQuery(id+"F0.wireOp",EDGE,"E1.0");var subQ4=sQuery(id+"F0.wireOp",EDGE,"E3.right");var subQ29=sQuery(id+"F1.wireOp",EDGE,"E12");Q46=makeQuery(id+"F7.boolean.opBoolean","INTERSECT",EDGE,{"derivedFrom":[makeQuery(id+"F5.boolean.opBoolean","MERGE",FACE,{"derivedFrom":[makeQuery(id+"F3.boolean.opBoolean","SPLIT",FACE,{"disambiguationData":[TD([makeQuery(id+"F3.opExtrude","SWEPT_FACE",FACE,{"disambiguationData":[OSD([subQ4])]})])],"derivedFrom":makeQuery(id+"F2.opExtrude","SWEPT_FACE",FACE,{"disambiguationData":[OSD([subQ29])]})}),makeQuery(id+"F5.opExtrude","SWEPT_FACE",FACE,{"disambiguationData":[OSD([subQ1]),TDD([makeQuery(id+"F0.imprint","IMPRINT",EDGE,{"disambiguationData":[TD([[makeQuery(id+"F0.imprint","INTERSECT",VERTEX,{"disambiguationData":[OD(1.0)],"derivedFrom":[subQ1,subQ4]}),-1.0]])],"derivedFrom":subQ1})])]}),makeQuery(id+"F5.opExtrude","SWEPT_FACE",FACE,{"disambiguationData":[OSD([subQ1]),TDD([makeQuery(id+"F0.imprint","IMPRINT",EDGE,{"disambiguationData":[TD([[makeQuery(id+"F0.imprint","INTERSECT",VERTEX,{"disambiguationData":[OD(1.0)],"derivedFrom":[subQ1,subQ0]}),-1.0]])],"derivedFrom":subQ1})])]})]}),makeQuery(id+"F7.opExtrude","SWEPT_FACE",FACE,{"disambiguationData":[OSD([sQuery(id+"F6.wireOp",EDGE,"E29")])]})]});}
            var Q47;
            {var subQ0=sQuery(id+"F0.wireOp",EDGE,"E3.right");Q47=makeQuery(id+"F7.boolean.opBoolean","INTERSECT",EDGE,{"derivedFrom":[makeQuery(id+"F5.boolean.opBoolean","MERGE",FACE,{"derivedFrom":[makeQuery(id+"F3.opExtrude","SWEPT_FACE",FACE,{"disambiguationData":[OSD([subQ0])]}),makeQuery(id+"F5.opExtrude","SWEPT_FACE",FACE,{"disambiguationData":[OSD([subQ0]),TDD([makeQuery(id+"F0.imprint","IMPRINT",EDGE,{"disambiguationData":[TD([[makeQuery(id+"F0.imprint","INTERSECT",VERTEX,{"disambiguationData":[OD(1.0)],"derivedFrom":[sQuery(id+"F0.wireOp",EDGE,"E1.0"),subQ0]}),1.0]])],"derivedFrom":subQ0})])]})]}),makeQuery(id+"F7.opExtrude","SWEPT_FACE",FACE,{"disambiguationData":[OSD([sQuery(id+"F6.wireOp",EDGE,"E29")])]})]});}
            var Q48;
            Q48=makeQuery(id+"F7.boolean.opBoolean","INTERSECT",EDGE,{"derivedFrom":[makeQuery(id+"F3.opExtrude","SWEPT_FACE",FACE,{"disambiguationData":[OSD([sQuery(id+"F0.wireOp",EDGE,"E3.left")])]}),makeQuery(id+"F7.opExtrude","SWEPT_FACE",FACE,{"disambiguationData":[OSD([sQuery(id+"F6.wireOp",EDGE,"E29")])]})]});
            var Q49;
            {var subQ2=sQuery(id+"F0.wireOp",EDGE,"E3.left");var subQ24=sQuery(id+"F1.wireOp",EDGE,"E12");Q49=makeQuery(id+"F7.boolean.opBoolean","INTERSECT",EDGE,{"derivedFrom":[makeQuery(id+"F3.boolean.opBoolean","SPLIT",FACE,{"disambiguationData":[TD([makeQuery(id+"F3.opExtrude","SWEPT_FACE",FACE,{"disambiguationData":[OSD([subQ2])]})])],"derivedFrom":makeQuery(id+"F2.opExtrude","SWEPT_FACE",FACE,{"disambiguationData":[OSD([subQ24])]})}),makeQuery(id+"F7.opExtrude","SWEPT_FACE",FACE,{"disambiguationData":[OSD([sQuery(id+"F6.wireOp",EDGE,"E29")])]})]});}
            fillet(context, id + "F8", {"entities" : qUnion([Q0, Q1, Q2, Q3, Q4, Q5, Q6, Q7, Q8, Q9, Q10, Q11, Q12, Q13, Q14, Q15, Q16, Q17, Q18, Q19, Q20, Q21, Q22, Q23, Q24, Q25, Q26, Q27, Q28, Q29, Q30, Q31, Q32, Q33, Q34, Q35, Q36, Q37, Q38, Q39, Q40, Q41, Q42, Q43, Q44, Q45, Q46, Q47, Q48, Q49]), "radius" : 1 * mm, "tangentPropagation" : true, "allowEdgeOverflow" : false});
        }
        {
            var Q0;
            {var subQ0=sQuery(id+"F6.wireOp",EDGE,"E31");var subQ1=sQuery(id+"F6.wireOp",EDGE,"E13");var subQ2=makeQuery(id+"F6.imprint","INTERSECT",VERTEX,{"disambiguationData":[OD(0.0)],"derivedFrom":[subQ1,subQ0]});Q0=makeQuery(id+"F6.imprint","IMPRINT",FACE,{"disambiguationData":[TD([[makeQuery(id+"F6.imprint","IMPRINT",EDGE,{"disambiguationData":[TD([[subQ2,-1.0]])],"derivedFrom":subQ1}),-1.0]])]});}
            var Q1;
            {var subQ0=sQuery(id+"F6.wireOp",EDGE,"E31");var subQ1=sQuery(id+"F6.wireOp",EDGE,"E13");var subQ2=makeQuery(id+"F6.imprint","INTERSECT",VERTEX,{"disambiguationData":[OD(0.0)],"derivedFrom":[subQ1,subQ0]});Q1=makeQuery(id+"F6.imprint","IMPRINT",FACE,{"disambiguationData":[TD([[makeQuery(id+"F6.imprint","IMPRINT",EDGE,{"disambiguationData":[TD([[subQ2,-1.0]])],"derivedFrom":subQ1}),1.0]])]});}
            var Q2;
            {var subQ0=sQuery(id+"F6.wireOp",EDGE,"E32");var subQ1=sQuery(id+"F6.wireOp",EDGE,"E13");var subQ2=makeQuery(id+"F6.imprint","INTERSECT",VERTEX,{"disambiguationData":[OD(0.0)],"derivedFrom":[subQ1,subQ0]});Q2=makeQuery(id+"F6.imprint","IMPRINT",FACE,{"disambiguationData":[TD([[makeQuery(id+"F6.imprint","IMPRINT",EDGE,{"disambiguationData":[TD([[subQ2,-1.0]])],"derivedFrom":subQ1}),-1.0]])]});}
            var Q3;
            {var subQ0=sQuery(id+"F6.wireOp",EDGE,"E32");var subQ1=sQuery(id+"F6.wireOp",EDGE,"E13");var subQ2=makeQuery(id+"F6.imprint","INTERSECT",VERTEX,{"disambiguationData":[OD(0.0)],"derivedFrom":[subQ1,subQ0]});Q3=makeQuery(id+"F6.imprint","IMPRINT",FACE,{"disambiguationData":[TD([[makeQuery(id+"F6.imprint","IMPRINT",EDGE,{"disambiguationData":[TD([[subQ2,-1.0]])],"derivedFrom":subQ1}),1.0]])]});}
            var Q4;
            {var subQ0=sQuery(id+"F6.wireOp",EDGE,"E33");var subQ1=sQuery(id+"F6.wireOp",EDGE,"E13");var subQ2=makeQuery(id+"F6.imprint","INTERSECT",VERTEX,{"disambiguationData":[OD(0.0)],"derivedFrom":[subQ1,subQ0]});Q4=makeQuery(id+"F6.imprint","IMPRINT",FACE,{"disambiguationData":[TD([[makeQuery(id+"F6.imprint","IMPRINT",EDGE,{"disambiguationData":[TD([[subQ2,-1.0]])],"derivedFrom":subQ1}),1.0]])]});}
            var Q5;
            {var subQ0=sQuery(id+"F6.wireOp",EDGE,"E33");var subQ1=sQuery(id+"F6.wireOp",EDGE,"E13");var subQ2=makeQuery(id+"F6.imprint","INTERSECT",VERTEX,{"disambiguationData":[OD(0.0)],"derivedFrom":[subQ1,subQ0]});Q5=makeQuery(id+"F6.imprint","IMPRINT",FACE,{"disambiguationData":[TD([[makeQuery(id+"F6.imprint","IMPRINT",EDGE,{"disambiguationData":[TD([[subQ2,-1.0]])],"derivedFrom":subQ1}),-1.0]])]});}
            var Q6;
            {var subQ0=sQuery(id+"F6.wireOp",EDGE,"E34");var subQ1=sQuery(id+"F6.wireOp",EDGE,"E13");var subQ2=makeQuery(id+"F6.imprint","INTERSECT",VERTEX,{"disambiguationData":[OD(0.0)],"derivedFrom":[subQ1,subQ0]});Q6=makeQuery(id+"F6.imprint","IMPRINT",FACE,{"disambiguationData":[TD([[makeQuery(id+"F6.imprint","IMPRINT",EDGE,{"disambiguationData":[TD([[subQ2,-1.0]])],"derivedFrom":subQ1}),1.0]])]});}
            var Q7;
            {var subQ0=sQuery(id+"F6.wireOp",EDGE,"E34");var subQ1=sQuery(id+"F6.wireOp",EDGE,"E13");var subQ2=makeQuery(id+"F6.imprint","INTERSECT",VERTEX,{"disambiguationData":[OD(0.0)],"derivedFrom":[subQ1,subQ0]});Q7=makeQuery(id+"F6.imprint","IMPRINT",FACE,{"disambiguationData":[TD([[makeQuery(id+"F6.imprint","IMPRINT",EDGE,{"disambiguationData":[TD([[subQ2,-1.0]])],"derivedFrom":subQ1}),-1.0]])]});}
            var Q8;
            {var subQ1=sQuery(id+"F6.wireOp",EDGE,"E36.bottom");Q8=makeQuery(id+"F6.imprint","IMPRINT",FACE,{"disambiguationData":[TD([[makeQuery(id+"F6.imprint","IMPRINT",EDGE,{"derivedFrom":subQ1}),-1.0]])]});}
            var Q9;
            {var subQ0=sQuery(id+"F6.wireOp",EDGE,"E36.top");var subQ1=sQuery(id+"F6.wireOp",EDGE,"E13");var subQ2=makeQuery(id+"F6.imprint","INTERSECT",VERTEX,{"derivedFrom":[subQ1,subQ0]});Q9=makeQuery(id+"F6.imprint","IMPRINT",FACE,{"disambiguationData":[TD([[makeQuery(id+"F6.imprint","IMPRINT",EDGE,{"disambiguationData":[TD([[subQ2,-1.0]])],"derivedFrom":subQ1}),1.0]])]});}
            var Q10;
            {var subQ0=sQuery(id+"F6.wireOp",EDGE,"E35");var subQ1=sQuery(id+"F6.wireOp",EDGE,"E13");var subQ2=makeQuery(id+"F6.imprint","INTERSECT",VERTEX,{"disambiguationData":[OD(0.0)],"derivedFrom":[subQ1,subQ0]});Q10=makeQuery(id+"F6.imprint","IMPRINT",FACE,{"disambiguationData":[TD([[makeQuery(id+"F6.imprint","IMPRINT",EDGE,{"disambiguationData":[TD([[subQ2,-1.0]])],"derivedFrom":subQ1}),-1.0]])]});}
            var Q11;
            {var subQ0=sQuery(id+"F6.wireOp",EDGE,"E35");var subQ1=sQuery(id+"F6.wireOp",EDGE,"E13");var subQ2=makeQuery(id+"F6.imprint","INTERSECT",VERTEX,{"disambiguationData":[OD(0.0)],"derivedFrom":[subQ1,subQ0]});Q11=makeQuery(id+"F6.imprint","IMPRINT",FACE,{"disambiguationData":[TD([[makeQuery(id+"F6.imprint","IMPRINT",EDGE,{"disambiguationData":[TD([[subQ2,-1.0]])],"derivedFrom":subQ1}),1.0]])]});}
            extrude(context, id + "F9", {"entities" : qUnion([Q0, Q1, Q2, Q3, Q4, Q5, Q6, Q7, Q8, Q9, Q10, Q11]), "operationType" : NewBodyOperationType.ADD, "depth" : 11 * mm, "offsetDistance" : 25 * mm, "hasDraft" : true, "draftAngle" : .9 * degree, "draftPullDirection" : true});
        }
        {
            var Q0;
            Q0=makeQuery(id+"F9.opExtrude","CAP_EDGE",EDGE,{"disambiguationData":[OSD([sQuery(id+"F6.wireOp",EDGE,"E35")])],"isStart":false});
            var Q1;
            Q1=makeQuery(id+"F9.opExtrude","CAP_FACE",FACE,{"disambiguationData":[OSD([sQuery(id+"F6.wireOp",EDGE,"E31")])],"isStart":false});
            var Q2;
            Q2=makeQuery(id+"F9.opExtrude","CAP_FACE",FACE,{"disambiguationData":[OSD([sQuery(id+"F6.wireOp",EDGE,"E32")])],"isStart":false});
            var Q3;
            Q3=makeQuery(id+"F9.opExtrude","CAP_FACE",FACE,{"disambiguationData":[OSD([sQuery(id+"F6.wireOp",EDGE,"E33")])],"isStart":false});
            var Q4;
            Q4=makeQuery(id+"F9.opExtrude","CAP_FACE",FACE,{"disambiguationData":[OSD([sQuery(id+"F6.wireOp",EDGE,"E34")])],"isStart":false});
            var Q5;
            Q5=makeQuery(id+"F9.opExtrude","CAP_EDGE",EDGE,{"disambiguationData":[OSD([sQuery(id+"F6.wireOp",EDGE,"E36.left")])],"isStart":false});
            var Q6;
            Q6=makeQuery(id+"F9.opExtrude","CAP_EDGE",EDGE,{"disambiguationData":[OSD([sQuery(id+"F6.wireOp",EDGE,"E36.right")])],"isStart":false});
            var Q7;
            Q7=makeQuery(id+"F9.opExtrude","CAP_EDGE",EDGE,{"disambiguationData":[OSD([sQuery(id+"F6.wireOp",EDGE,"E36.bottom")])],"isStart":false});
            var Q8;
            Q8=makeQuery(id+"F9.opExtrude","CAP_EDGE",EDGE,{"disambiguationData":[OSD([sQuery(id+"F6.wireOp",EDGE,"E36.top")])],"isStart":false});
            fillet(context, id + "F10", {"entities" : qUnion([Q0, Q1, Q2, Q3, Q4, Q5, Q6, Q7, Q8]), "radius" : .45 * mm, "tangentPropagation" : true, "allowEdgeOverflow" : false});
        }
        {
            var Q0;
            {var subQ0=sQuery(id+"F6.wireOp",EDGE,"E35");var subQ1=sQuery(id+"F6.wireOp",EDGE,"E13");var subQ2=makeQuery(id+"F6.imprint","INTERSECT",VERTEX,{"disambiguationData":[OD(0.0)],"derivedFrom":[subQ1,subQ0]});Q0=makeQuery(id+"F6.imprint","IMPRINT",FACE,{"disambiguationData":[TD([[makeQuery(id+"F6.imprint","IMPRINT",EDGE,{"disambiguationData":[TD([[subQ2,-1.0]])],"derivedFrom":subQ1}),-1.0]])]});}
            var Q1;
            {var subQ0=sQuery(id+"F6.wireOp",EDGE,"E35");var subQ1=sQuery(id+"F6.wireOp",EDGE,"E13");var subQ2=makeQuery(id+"F6.imprint","INTERSECT",VERTEX,{"disambiguationData":[OD(0.0)],"derivedFrom":[subQ1,subQ0]});Q1=makeQuery(id+"F6.imprint","IMPRINT",FACE,{"disambiguationData":[TD([[makeQuery(id+"F6.imprint","IMPRINT",EDGE,{"disambiguationData":[TD([[subQ2,-1.0]])],"derivedFrom":subQ1}),1.0]])]});}
            var Q2;
            {var subQ1=sQuery(id+"F6.wireOp",EDGE,"E36.bottom");Q2=makeQuery(id+"F6.imprint","IMPRINT",FACE,{"disambiguationData":[TD([[makeQuery(id+"F6.imprint","IMPRINT",EDGE,{"derivedFrom":subQ1}),-1.0]])]});}
            var Q3;
            {var subQ0=sQuery(id+"F6.wireOp",EDGE,"E36.top");var subQ1=sQuery(id+"F6.wireOp",EDGE,"E13");var subQ2=makeQuery(id+"F6.imprint","INTERSECT",VERTEX,{"derivedFrom":[subQ1,subQ0]});Q3=makeQuery(id+"F6.imprint","IMPRINT",FACE,{"disambiguationData":[TD([[makeQuery(id+"F6.imprint","IMPRINT",EDGE,{"disambiguationData":[TD([[subQ2,-1.0]])],"derivedFrom":subQ1}),1.0]])]});}
            var Q4;
            {var subQ0=sQuery(id+"F6.wireOp",EDGE,"E34");var subQ1=sQuery(id+"F6.wireOp",EDGE,"E13");var subQ2=makeQuery(id+"F6.imprint","INTERSECT",VERTEX,{"disambiguationData":[OD(0.0)],"derivedFrom":[subQ1,subQ0]});Q4=makeQuery(id+"F6.imprint","IMPRINT",FACE,{"disambiguationData":[TD([[makeQuery(id+"F6.imprint","IMPRINT",EDGE,{"disambiguationData":[TD([[subQ2,-1.0]])],"derivedFrom":subQ1}),1.0]])]});}
            var Q5;
            {var subQ0=sQuery(id+"F6.wireOp",EDGE,"E34");var subQ1=sQuery(id+"F6.wireOp",EDGE,"E13");var subQ2=makeQuery(id+"F6.imprint","INTERSECT",VERTEX,{"disambiguationData":[OD(0.0)],"derivedFrom":[subQ1,subQ0]});Q5=makeQuery(id+"F6.imprint","IMPRINT",FACE,{"disambiguationData":[TD([[makeQuery(id+"F6.imprint","IMPRINT",EDGE,{"disambiguationData":[TD([[subQ2,-1.0]])],"derivedFrom":subQ1}),-1.0]])]});}
            var Q6;
            {var subQ0=sQuery(id+"F6.wireOp",EDGE,"E33");var subQ1=sQuery(id+"F6.wireOp",EDGE,"E13");var subQ2=makeQuery(id+"F6.imprint","INTERSECT",VERTEX,{"disambiguationData":[OD(0.0)],"derivedFrom":[subQ1,subQ0]});Q6=makeQuery(id+"F6.imprint","IMPRINT",FACE,{"disambiguationData":[TD([[makeQuery(id+"F6.imprint","IMPRINT",EDGE,{"disambiguationData":[TD([[subQ2,-1.0]])],"derivedFrom":subQ1}),1.0]])]});}
            var Q7;
            {var subQ0=sQuery(id+"F6.wireOp",EDGE,"E33");var subQ1=sQuery(id+"F6.wireOp",EDGE,"E13");var subQ2=makeQuery(id+"F6.imprint","INTERSECT",VERTEX,{"disambiguationData":[OD(0.0)],"derivedFrom":[subQ1,subQ0]});Q7=makeQuery(id+"F6.imprint","IMPRINT",FACE,{"disambiguationData":[TD([[makeQuery(id+"F6.imprint","IMPRINT",EDGE,{"disambiguationData":[TD([[subQ2,-1.0]])],"derivedFrom":subQ1}),-1.0]])]});}
            var Q8;
            {var subQ0=sQuery(id+"F6.wireOp",EDGE,"E32");var subQ1=sQuery(id+"F6.wireOp",EDGE,"E13");var subQ2=makeQuery(id+"F6.imprint","INTERSECT",VERTEX,{"disambiguationData":[OD(0.0)],"derivedFrom":[subQ1,subQ0]});Q8=makeQuery(id+"F6.imprint","IMPRINT",FACE,{"disambiguationData":[TD([[makeQuery(id+"F6.imprint","IMPRINT",EDGE,{"disambiguationData":[TD([[subQ2,-1.0]])],"derivedFrom":subQ1}),1.0]])]});}
            var Q9;
            {var subQ0=sQuery(id+"F6.wireOp",EDGE,"E32");var subQ1=sQuery(id+"F6.wireOp",EDGE,"E13");var subQ2=makeQuery(id+"F6.imprint","INTERSECT",VERTEX,{"disambiguationData":[OD(0.0)],"derivedFrom":[subQ1,subQ0]});Q9=makeQuery(id+"F6.imprint","IMPRINT",FACE,{"disambiguationData":[TD([[makeQuery(id+"F6.imprint","IMPRINT",EDGE,{"disambiguationData":[TD([[subQ2,-1.0]])],"derivedFrom":subQ1}),-1.0]])]});}
            var Q10;
            {var subQ0=sQuery(id+"F6.wireOp",EDGE,"E31");var subQ1=sQuery(id+"F6.wireOp",EDGE,"E13");var subQ2=makeQuery(id+"F6.imprint","INTERSECT",VERTEX,{"disambiguationData":[OD(0.0)],"derivedFrom":[subQ1,subQ0]});Q10=makeQuery(id+"F6.imprint","IMPRINT",FACE,{"disambiguationData":[TD([[makeQuery(id+"F6.imprint","IMPRINT",EDGE,{"disambiguationData":[TD([[subQ2,-1.0]])],"derivedFrom":subQ1}),-1.0]])]});}
            var Q11;
            {var subQ0=sQuery(id+"F6.wireOp",EDGE,"E31");var subQ1=sQuery(id+"F6.wireOp",EDGE,"E13");var subQ2=makeQuery(id+"F6.imprint","INTERSECT",VERTEX,{"disambiguationData":[OD(0.0)],"derivedFrom":[subQ1,subQ0]});Q11=makeQuery(id+"F6.imprint","IMPRINT",FACE,{"disambiguationData":[TD([[makeQuery(id+"F6.imprint","IMPRINT",EDGE,{"disambiguationData":[TD([[subQ2,-1.0]])],"derivedFrom":subQ1}),1.0]])]});}
            extrude(context, id + "F11", {"entities" : qUnion([Q0, Q1, Q2, Q3, Q4, Q5, Q6, Q7, Q8, Q9, Q10, Q11]), "operationType" : NewBodyOperationType.REMOVE, "depth" : 3 * mm, "offsetDistance" : 25 * mm});
        }
        {
            var Q0;
            Q0=qCreatedBy(makeId("Top.planeOp"),FACE);
            var sketch = newSketch(context, id + "F12", { "sketchPlane" : qUnion([Q0])});
            skCircle(sketch, "E37", {"center": v(0, 0) * mm, "radius": 17.33 * mm});
            skSolve(sketch);
        }
        {
            var Q0;
            Q0=qSketchRegion(id+"F12",true);
            extrude(context, id + "F13", {"entities" : qUnion([Q0]), "operationType" : NewBodyOperationType.REMOVE, "depth" : 1 * mm, "offsetDistance" : 25 * mm});
        }
    });
